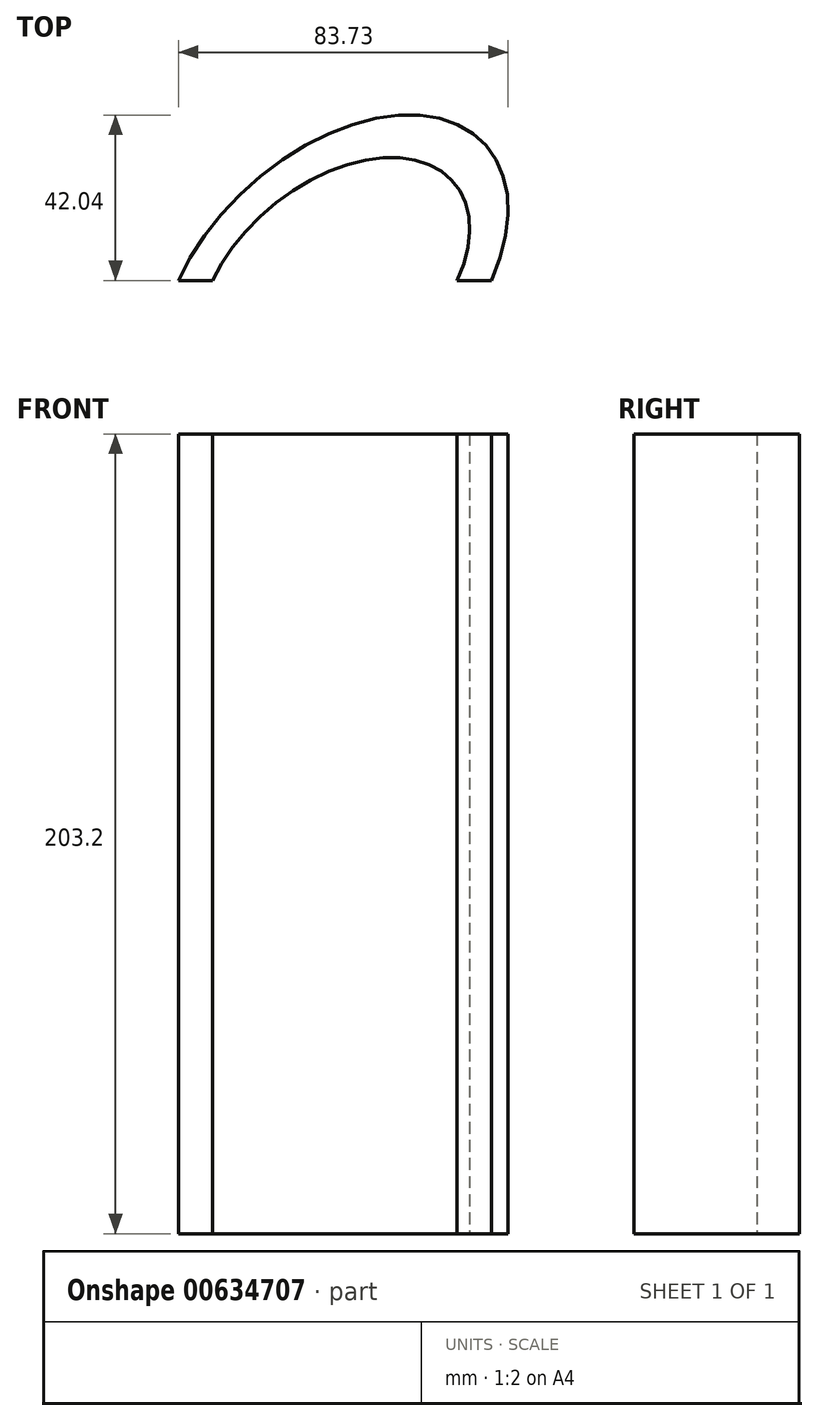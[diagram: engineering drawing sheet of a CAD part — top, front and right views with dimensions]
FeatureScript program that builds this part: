
annotation { "Feature Type Name" : "Feature", "Feature Type Description" : "" }
export const myFeature = defineFeature(function(context is Context, id is Id, definition is map)
    precondition{}
    {
        {
            var Q0;
            Q0=qCreatedBy(makeId("Top.planeOp"),FACE);
            var sketch = newSketch(context, id + "F0", { "sketchPlane" : qUnion([Q0])});
            skEllipse(sketch, "E0", {"center": v(0, 0) * mm, "majorRadius": 51.47 * mm, "minorRadius": 32.46 * mm, "majorAxis": v(-0.74, -0.67)});
            skSolve(sketch);
        }
        {
            var Q0;
            Q0=makeQuery(id+"F0.imprint","IMPRINT",FACE,{"disambiguationData":[TD([[makeQuery(id+"F0.imprint","IMPRINT",EDGE,{"derivedFrom":sQuery(id+"F0.wireOp",EDGE,"E0")}),1.0]])]});
            extrude(context, id + "F1", {"entities" : qUnion([Q0]), "depth" : 203.2 * mm, "offsetDistance" : 25.4 * mm});
        }
        {
            var Q0;
            Q0=makeQuery(id+"F1.opExtrude","CAP_FACE",FACE,{"disambiguationData":[OSD([sQuery(id+"F0.wireOp",EDGE,"E0")])],"isStart":true});
            var sketch = newSketch(context, id + "F2", { "sketchPlane" : qUnion([Q0])});
            skEllipse(sketch, "E1", {"center": v(0, 0) * mm, "majorRadius": 38.92 * mm, "minorRadius": 25.2 * mm, "majorAxis": v(-0.78, 0.63)});
            skSolve(sketch);
        }
        {
            var Q0;
            Q0=makeQuery(id+"F2.imprint","IMPRINT",FACE,{"disambiguationData":[TD([[makeQuery(id+"F2.imprint","IMPRINT",EDGE,{"derivedFrom":sQuery(id+"F2.wireOp",EDGE,"E1")}),1.0]])]});
            var sketch = newSketch(context, id + "F3", { "sketchPlane" : qUnion([Q0])});
            skEllipse(sketch, "E2", {"center": v(0, 0) * mm, "majorRadius": 39.13 * mm, "minorRadius": 24.76 * mm, "majorAxis": v(-0.78, 0.63)});
            skSolve(sketch);
        }
        {
            var Q0;
            Q0 = qSketchRegion(id + "F3", true);
            extrude(context, id + "F4", {"entities" : qUnion([Q0]), "operationType" : NewBodyOperationType.REMOVE, "endBound" : BoundingType.THROUGH_ALL, "oppositeDirection" : true, "depth" : 25.4 * mm, "offsetDistance" : 25.4 * mm});
        }
        {
            var Q0;
            Q0=qCreatedBy(makeId("Front.planeOp"),FACE);
            var sketch = newSketch(context, id + "F5", { "sketchPlane" : qUnion([Q0])});
            skLineSegment(sketch, "E3.bottom", {"start": v(-156.42, -78.16) * mm, "end": v(130.1, -78.16) * mm});
            skLineSegment(sketch, "E3.top", {"start": v(-156.42, 223.17) * mm, "end": v(130.1, 223.17) * mm});
            skLineSegment(sketch, "E3.left", {"start": v(-156.42, -78.16) * mm, "end": v(-156.42, 223.17) * mm});
            skLineSegment(sketch, "E3.right", {"start": v(130.1, -78.16) * mm, "end": v(130.1, 223.17) * mm});
            skSolve(sketch);
        }
        {
            var Q0;
            Q0=makeQuery(id+"F5.imprint","IMPRINT",FACE,{"disambiguationData":[TD([[makeQuery(id+"F5.imprint","IMPRINT",EDGE,{"derivedFrom":sQuery(id+"F5.wireOp",EDGE,"E3.bottom")}),1.0]])]});
            extrude(context, id + "F6", {"entities" : qUnion([Q0]), "operationType" : NewBodyOperationType.REMOVE, "depth" : 76.2 * mm, "offsetDistance" : 25.4 * mm});
        }
    });
